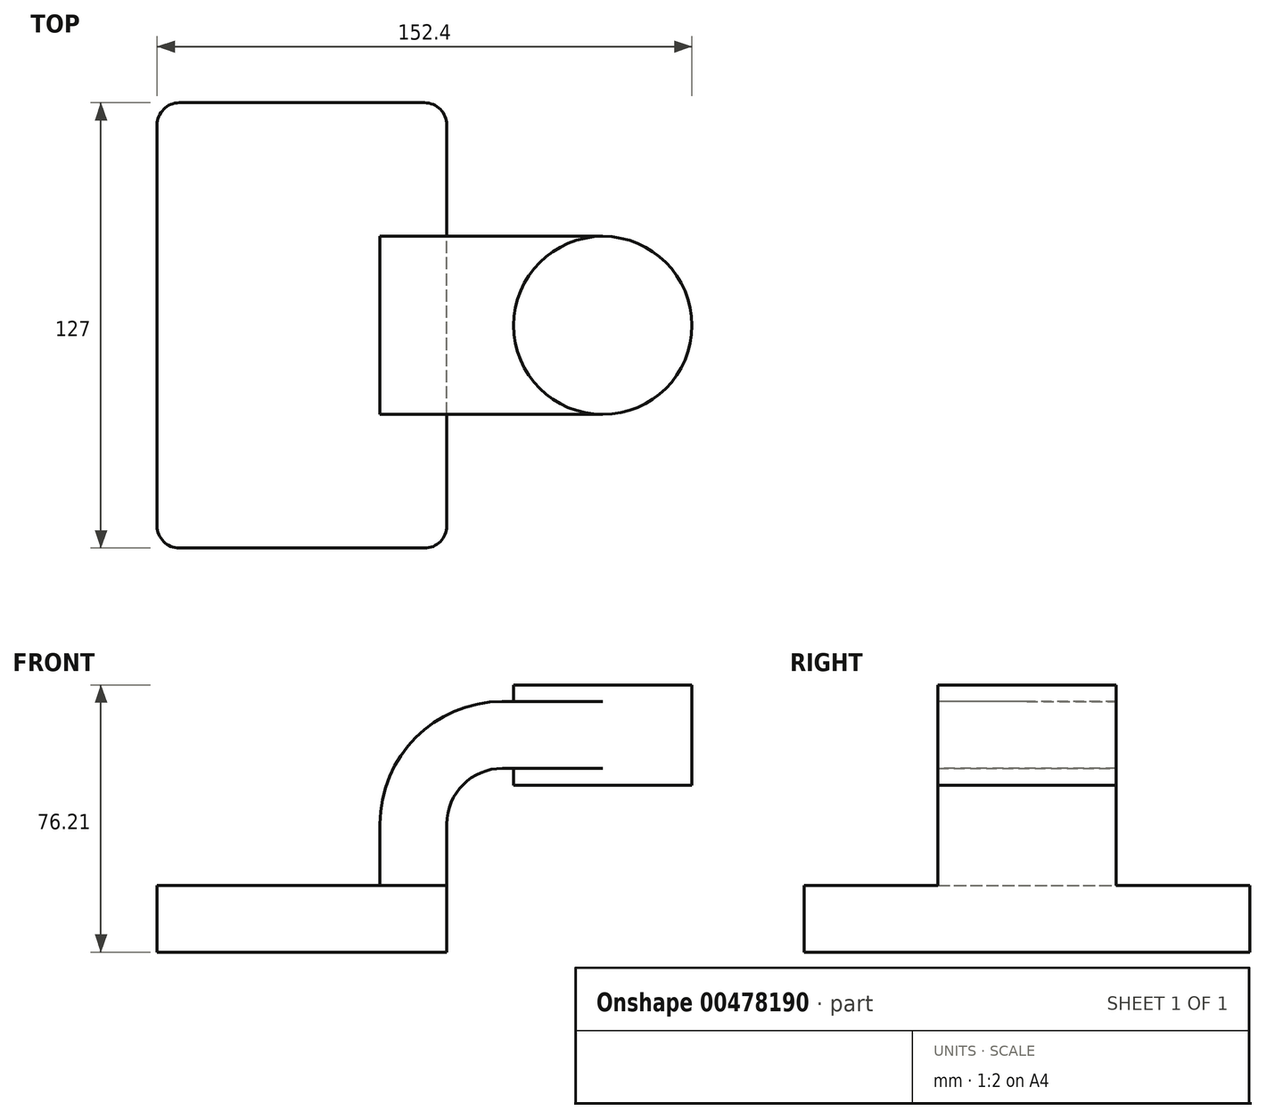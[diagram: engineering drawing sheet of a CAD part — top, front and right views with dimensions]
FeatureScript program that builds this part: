
annotation { "Feature Type Name" : "Feature", "Feature Type Description" : "" }
export const myFeature = defineFeature(function(context is Context, id is Id, definition is map)
    precondition{}
    {
        {
            var Q0;
            Q0=qCreatedBy(makeId("Front.planeOp"),FACE);
            var sketch = newSketch(context, id + "F0", { "sketchPlane" : qUnion([Q0])});
            skLineSegment(sketch, "E0.bottom", {"start": v(41.27, 9.53) * mm, "end": v(-41.28, 9.53) * mm});
            skLineSegment(sketch, "E0.top", {"start": v(41.28, -9.52) * mm, "end": v(-41.27, -9.52) * mm});
            skLineSegment(sketch, "E0.left", {"start": v(41.28, 9.53) * mm, "end": v(41.28, -9.52) * mm});
            skLineSegment(sketch, "E0.right", {"start": v(-41.28, 9.53) * mm, "end": v(-41.27, -9.52) * mm});
            skPoint(sketch, "E0.middle", {"position": v(0, 0) * mm});
            skLineSegment(sketch, "E1.bottom", {"start": v(111.13, 38.1) * mm, "end": v(60.33, 38.1) * mm});
            skLineSegment(sketch, "E1.top", {"start": v(111.13, 66.68) * mm, "end": v(60.33, 66.68) * mm});
            skLineSegment(sketch, "E1.left", {"start": v(111.13, 38.1) * mm, "end": v(111.13, 66.68) * mm});
            skLineSegment(sketch, "E1.right", {"start": v(60.33, 38.1) * mm, "end": v(60.33, 66.68) * mm});
            skPoint(sketch, "E1.middle", {"position": v(85.73, 52.39) * mm});
            skLineSegment(sketch, "E2", {"start": v(41.27, 9.53) * mm, "end": v(41.27, 27) * mm});
            skArc(sketch, "E3", {"start": v(41.27, 27) * mm, "mid": v(45.92, 38.23) * mm, "end": v(57.15, 42.88) * mm});
            skLineSegment(sketch, "E4", {"start": v(57.15, 42.88) * mm, "end": v(85.73, 42.88) * mm});
            skLineSegment(sketch, "E5.0", {"start": v(57.15, 61.93) * mm, "end": v(85.73, 61.93) * mm});
            skArc(sketch, "E5.1", {"start": v(22.23, 27) * mm, "mid": v(32.45, 51.7) * mm, "end": v(57.15, 61.93) * mm});
            skLineSegment(sketch, "E5.2", {"start": v(22.23, 9.53) * mm, "end": v(22.23, 27) * mm});
            skFitSpline(sketch, "E6", {"points": [v(57.15, 61.93) * mm, v(-41.28, 9.53) * mm], "startDerivative": vector(-104.28, -0.2) * mm, "endDerivative": vector(-86.28, -125.6) * mm});
            skLineSegment(sketch, "E7", {"start": v(85.73, 66.68) * mm, "end": v(85.73, 38.1) * mm});
            skSolve(sketch);
        }
        {
            var Q0;
            Q0=makeQuery(id+"F0.imprint","IMPRINT",FACE,{"disambiguationData":[TD([[makeQuery(id+"F0.imprint","IMPRINT",EDGE,{"derivedFrom":sQuery(id+"F0.wireOp",EDGE,"E0.top")}),-1.0]])]});
            extrude(context, id + "F1", {"entities" : qUnion([Q0]), "endBound" : BoundingType.SYMMETRIC, "depth" : 127 * mm});
        }
        {
            var Q0;
            {var subQ1=sQuery(id+"F0.wireOp",EDGE,"E2");Q0=makeQuery(id+"F0.imprint","IMPRINT",FACE,{"disambiguationData":[TD([[makeQuery(id+"F0.imprint","IMPRINT",EDGE,{"derivedFrom":subQ1}),1.0]])]});}
            var Q1;
            {var subQ0=sQuery(id+"F0.wireOp",EDGE,"E4");var subQ1=sQuery(id+"F0.wireOp",EDGE,"E1.right");var subQ2=makeQuery(id+"F0.imprint","INTERSECT",VERTEX,{"derivedFrom":[subQ1,subQ0]});Q1=makeQuery(id+"F0.imprint","IMPRINT",FACE,{"disambiguationData":[TD([[makeQuery(id+"F0.imprint","IMPRINT",EDGE,{"disambiguationData":[TD([[subQ2,-1.0]])],"derivedFrom":subQ1}),-1.0]])]});}
            extrude(context, id + "F2", {"entities" : qUnion([Q0, Q1]), "operationType" : NewBodyOperationType.ADD, "endBound" : BoundingType.SYMMETRIC, "depth" : 50.8 * mm});
        }
        {
            var Q0;
            {var subQ4=sQuery(id+"F0.wireOp",EDGE,"E5.1");Q0=makeQuery(id+"F0.imprint","IMPRINT",FACE,{"disambiguationData":[TD([[makeQuery(id+"F0.imprint","IMPRINT",EDGE,{"derivedFrom":subQ4}),1.0]])]});}
            extrude(context, id + "F3", {"entities" : qUnion([Q0]), "operationType" : NewBodyOperationType.ADD, "endBound" : BoundingType.SYMMETRIC, "depth" : 1 / 50.8 * mm});
        }
        {
            var Q0;
            {var subQ4=sQuery(id+"F0.wireOp",EDGE,"E1.left");Q0=makeQuery(id+"F0.imprint","IMPRINT",FACE,{"disambiguationData":[TD([[makeQuery(id+"F0.imprint","IMPRINT",EDGE,{"derivedFrom":subQ4}),1.0]])]});}
            var Q1;
            Q1=sQuery(id+"F0.wireOp",EDGE,"E7");
            revolve(context, id + "F4", {"operationType" : NewBodyOperationType.ADD, "entities" : qUnion([Q0]), "axis" : qUnion([Q1]), "revolveType" : RevolveType.FULL});
        }
        {
            var Q0;
            Q0=makeQuery(id+"F1.opExtrude","CAP_EDGE",EDGE,{"disambiguationData":[OSD([sQuery(id+"F0.wireOp",EDGE,"E0.right")])],"isStart":false});
            var Q1;
            Q1=makeQuery(id+"F1.opExtrude","CAP_EDGE",EDGE,{"disambiguationData":[OSD([sQuery(id+"F0.wireOp",EDGE,"E0.left")])],"isStart":false});
            var Q2;
            Q2=makeQuery(id+"F1.opExtrude","CAP_EDGE",EDGE,{"disambiguationData":[OSD([sQuery(id+"F0.wireOp",EDGE,"E0.left")])],"isStart":true});
            var Q3;
            Q3=makeQuery(id+"F1.opExtrude","CAP_EDGE",EDGE,{"disambiguationData":[OSD([sQuery(id+"F0.wireOp",EDGE,"E0.right")])],"isStart":true});
            fillet(context, id + "F5", {"entities" : qUnion([Q0, Q1, Q2, Q3]), "radius" : 6.35 * mm, "tangentPropagation" : true, "allowEdgeOverflow" : false});
        }
    });
